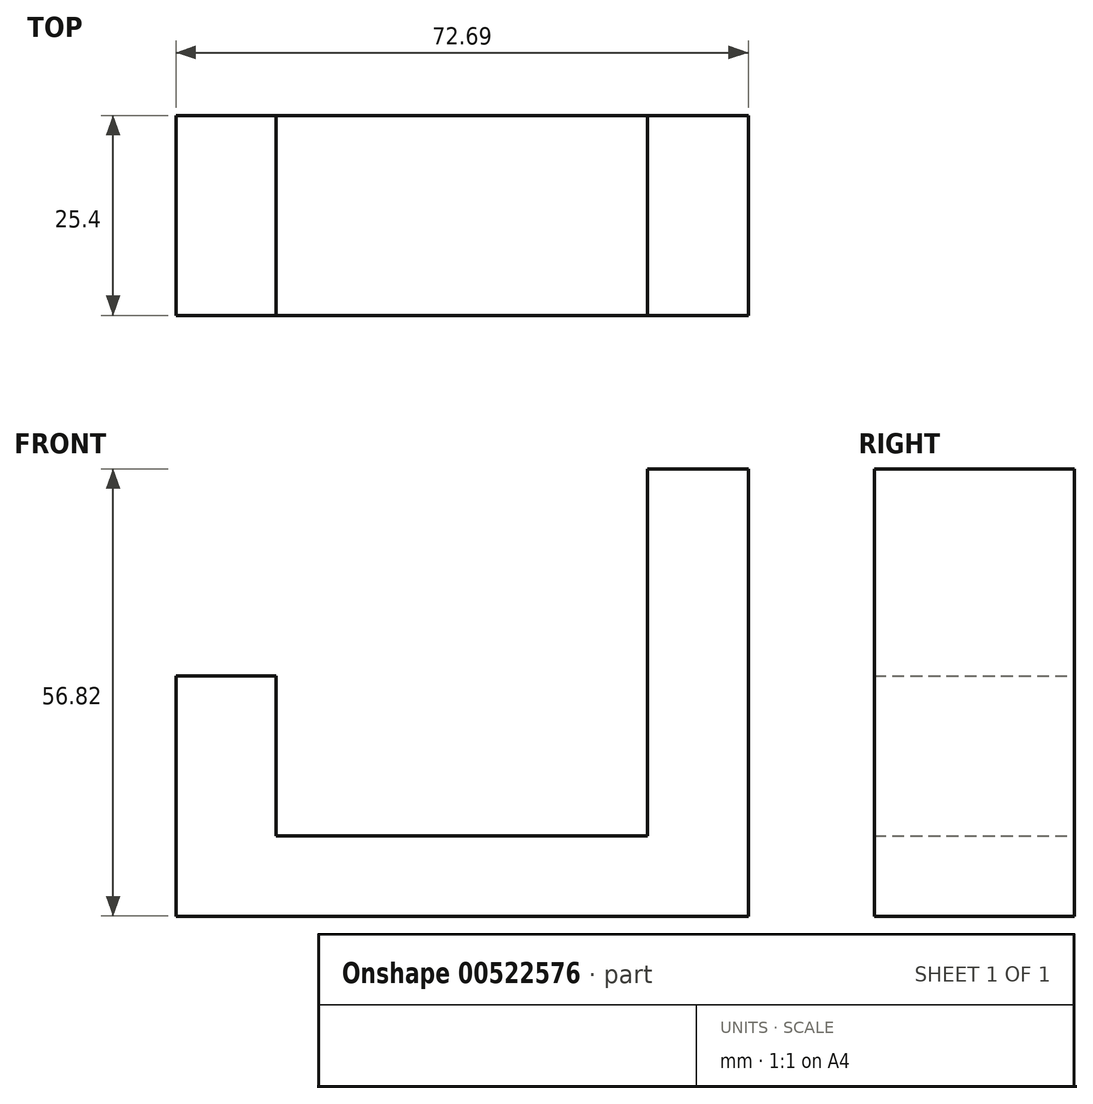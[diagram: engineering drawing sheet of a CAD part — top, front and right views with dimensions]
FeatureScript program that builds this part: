
annotation { "Feature Type Name" : "Feature", "Feature Type Description" : "" }
export const myFeature = defineFeature(function(context is Context, id is Id, definition is map)
    precondition{}
    {
        {
            var Q0;
            Q0=qCreatedBy(makeId("Front.planeOp"),FACE);
            var sketch = newSketch(context, id + "F0", { "sketchPlane" : qUnion([Q0])});
            skLineSegment(sketch, "E0.bottom", {"start": v(-59.9, 45.78) * mm, "end": v(-47.2, 45.78) * mm});
            skLineSegment(sketch, "E0.left", {"start": v(-59.9, 45.78) * mm, "end": v(-59.9, 25.46) * mm});
            skLineSegment(sketch, "E0.right", {"start": v(-47.2, 45.78) * mm, "end": v(-47.2, 25.46) * mm});
            skLineSegment(sketch, "E1.bottom", {"start": v(-47.2, 25.46) * mm, "end": v(0, 25.46) * mm});
            skLineSegment(sketch, "E1.top", {"start": v(-47.2, 15.3) * mm, "end": v(0, 15.3) * mm});
            skLineSegment(sketch, "E2.bottom", {"start": v(-47.2, 15.3) * mm, "end": v(-59.9, 15.3) * mm});
            skLineSegment(sketch, "E2.right", {"start": v(-59.9, 15.3) * mm, "end": v(-59.9, 25.46) * mm});
            skLineSegment(sketch, "E3.bottom", {"start": v(0, 15.3) * mm, "end": v(12.8, 15.3) * mm});
            skLineSegment(sketch, "E3.top", {"start": v(0, 72.12) * mm, "end": v(12.8, 72.12) * mm});
            skLineSegment(sketch, "E3.right", {"start": v(12.8, 15.3) * mm, "end": v(12.8, 72.12) * mm});
            skLineSegment(sketch, "E4", {"start": v(0, 72.12) * mm, "end": v(0, 25.46) * mm});
            skSolve(sketch);
        }
        {
            var Q0;
            Q0 = qSketchRegion(id + "F0", true);
            extrude(context, id + "F1", {"entities" : qUnion([Q0]), "depth" : 25.4 * mm, "offsetDistance" : 25.4 * mm});
        }
    });
